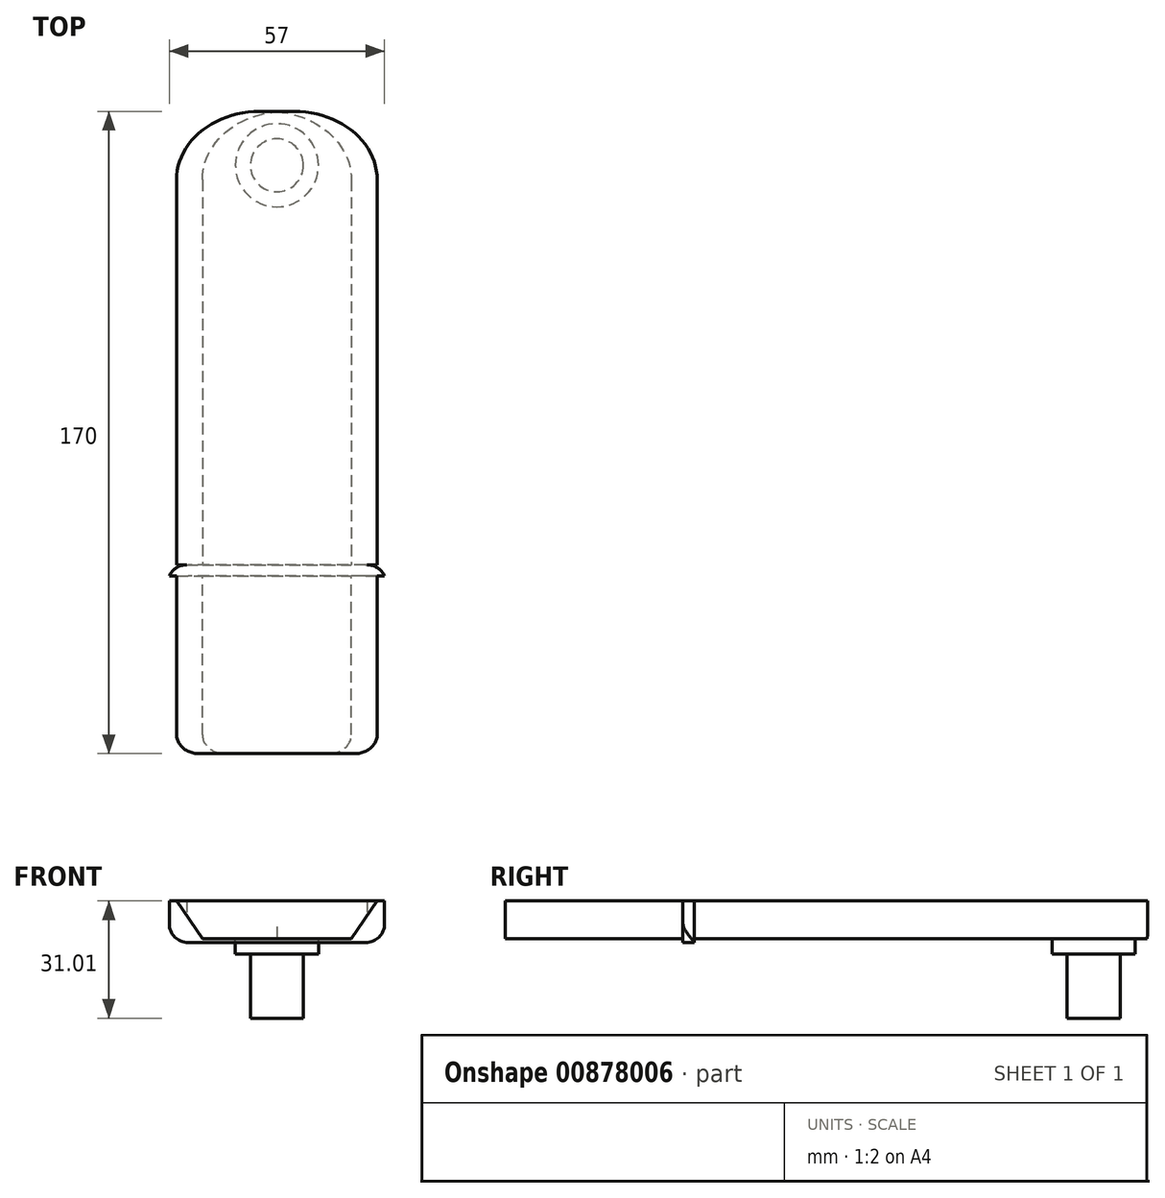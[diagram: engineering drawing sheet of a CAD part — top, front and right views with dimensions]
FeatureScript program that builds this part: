
annotation { "Feature Type Name" : "Feature", "Feature Type Description" : "" }
export const myFeature = defineFeature(function(context is Context, id is Id, definition is map)
    precondition{}
    {
        {
            var Q0;
            Q0=qCreatedBy(makeId("Front.planeOp"),FACE);
            var sketch = newSketch(context, id + "F0", { "sketchPlane" : qUnion([Q0])});
            skLineSegment(sketch, "E0.bottom", {"start": v(-20, -6.88) * mm, "end": v(20, -6.87) * mm});
            skLineSegment(sketch, "E1", {"start": v(27.5, 4.13) * mm, "end": v(20, -6.88) * mm});
            skLineSegment(sketch, "E2", {"start": v(-27.5, 4.12) * mm, "end": v(-20, -6.88) * mm});
            skLineSegment(sketch, "E3", {"start": v(-27.5, 4.12) * mm, "end": v(27.5, 4.13) * mm});
            skLineSegment(sketch, "E4.0", {"start": v(-27.5, 3.62) * mm, "end": v(27.5, 3.63) * mm});
            skLineSegment(sketch, "E5.0", {"start": v(-27.09, 4.4) * mm, "end": v(-19.59, -6.6) * mm});
            skLineSegment(sketch, "E6.0", {"start": v(-20, -6.38) * mm, "end": v(20, -6.37) * mm});
            skLineSegment(sketch, "E7.0", {"start": v(27.09, 4.4) * mm, "end": v(19.59, -6.6) * mm});
            skLineSegment(sketch, "E8.bottom", {"start": v(28.5, 3.63) * mm, "end": v(-28.5, 3.63) * mm});
            skLineSegment(sketch, "E8.top", {"start": v(28.5, -7.37) * mm, "end": v(-28.5, -7.38) * mm});
            skLineSegment(sketch, "E8.left", {"start": v(28.5, 3.63) * mm, "end": v(28.5, -7.37) * mm});
            skLineSegment(sketch, "E8.right", {"start": v(-28.5, 3.63) * mm, "end": v(-28.5, -7.38) * mm});
            skSolve(sketch);
        }
        {
            var Q0;
            {var subQ0=sQuery(id+"F0.wireOp",EDGE,"E5.0");var subQ1=sQuery(id+"F0.wireOp",EDGE,"E4.0");var subQ2=makeQuery(id+"F0.imprint","INTERSECT",VERTEX,{"derivedFrom":[subQ1,subQ0]});Q0=makeQuery(id+"F0.imprint","IMPRINT",FACE,{"disambiguationData":[TD([[makeQuery(id+"F0.imprint","IMPRINT",EDGE,{"disambiguationData":[TD([[subQ2,-1.0]])],"derivedFrom":subQ1}),-1.0]])]});}
            var Q1;
            {var subQ0=sQuery(id+"F0.wireOp",EDGE,"E6.0");var subQ1=sQuery(id+"F0.wireOp",EDGE,"E5.0");var subQ2=makeQuery(id+"F0.imprint","INTERSECT",VERTEX,{"derivedFrom":[subQ1,subQ0]});Q1=makeQuery(id+"F0.imprint","IMPRINT",FACE,{"disambiguationData":[TD([[makeQuery(id+"F0.imprint","IMPRINT",EDGE,{"disambiguationData":[TD([[subQ2,1.0]])],"derivedFrom":subQ1}),1.0]])]});}
            extrude(context, id + "F1", {"entities" : qUnion([Q0, Q1]), "depth" : 50 * mm, "offsetDistance" : 25 * mm});
        }
        {
            var Q0;
            {var subQ4=sQuery(id+"F0.wireOp",EDGE,"E0.bottom");Q0=makeQuery(id+"F0.imprint","IMPRINT",FACE,{"disambiguationData":[TD([[makeQuery(id+"F0.imprint","IMPRINT",EDGE,{"derivedFrom":subQ4}),-1.0]])]});}
            var Q1;
            {var subQ0=sQuery(id+"F0.wireOp",EDGE,"E6.0");var subQ1=sQuery(id+"F0.wireOp",EDGE,"E5.0");var subQ2=makeQuery(id+"F0.imprint","INTERSECT",VERTEX,{"derivedFrom":[subQ1,subQ0]});Q1=makeQuery(id+"F0.imprint","IMPRINT",FACE,{"disambiguationData":[TD([[makeQuery(id+"F0.imprint","IMPRINT",EDGE,{"disambiguationData":[TD([[subQ2,1.0]])],"derivedFrom":subQ1}),1.0]])]});}
            var Q2;
            {var subQ6=sQuery(id+"F0.wireOp",EDGE,"E0.bottom");Q2=makeQuery(id+"F0.imprint","IMPRINT",FACE,{"disambiguationData":[TD([[makeQuery(id+"F0.imprint","IMPRINT",EDGE,{"derivedFrom":subQ6}),1.0]])]});}
            extrude(context, id + "F2", {"entities" : qUnion([Q0, Q1, Q2]), "operationType" : NewBodyOperationType.ADD, "depth" : 3 * mm, "offsetDistance" : 25 * mm});
        }
        {
            var Q0;
            Q0=makeQuery(id+"F2.opExtrude","SWEPT_EDGE",EDGE,{"disambiguationData":[OSD([sQuery(id+"F0.wireOp",EDGE,"E8.top"),sQuery(id+"F0.wireOp",EDGE,"E8.left")])]});
            var Q1;
            Q1=makeQuery(id+"F2.opExtrude","SWEPT_EDGE",EDGE,{"disambiguationData":[OSD([sQuery(id+"F0.wireOp",EDGE,"E8.top"),sQuery(id+"F0.wireOp",EDGE,"E8.right")])]});
            var Q2;
            Q2=makeQuery(id+"F2.opExtrude","CAP_EDGE",EDGE,{"disambiguationData":[OSD([sQuery(id+"F0.wireOp",EDGE,"E8.left")])],"isStart":true});
            var Q3;
            Q3=makeQuery(id+"F2.opExtrude","CAP_EDGE",EDGE,{"disambiguationData":[OSD([sQuery(id+"F0.wireOp",EDGE,"E8.right")])],"isStart":true});
            fillet(context, id + "F3", {"entities" : qUnion([Q0, Q1, Q2, Q3]), "radius" : 5 * mm, "tangentPropagation" : true, "allowEdgeOverflow" : false});
        }
        {
            var Q0;
            {var subQ0=sQuery(id+"F0.wireOp",EDGE,"E6.0");var subQ1=sQuery(id+"F0.wireOp",EDGE,"E5.0");var subQ2=makeQuery(id+"F0.imprint","INTERSECT",VERTEX,{"derivedFrom":[subQ1,subQ0]});Q0=makeQuery(id+"F0.imprint","IMPRINT",FACE,{"disambiguationData":[TD([[makeQuery(id+"F0.imprint","IMPRINT",EDGE,{"disambiguationData":[TD([[subQ2,1.0]])],"derivedFrom":subQ1}),1.0]])]});}
            extrude(context, id + "F4", {"entities" : qUnion([Q0]), "operationType" : NewBodyOperationType.ADD, "oppositeDirection" : true, "depth" : 120 * mm, "offsetDistance" : 25 * mm});
        }
        {
            var Q0;
            Q0=makeQuery(id+"F4.opExtrude","CAP_EDGE",EDGE,{"disambiguationData":[OSD([sQuery(id+"F0.wireOp",EDGE,"E7.0")])],"isStart":false});
            var Q1;
            Q1=makeQuery(id+"F4.opExtrude","CAP_EDGE",EDGE,{"disambiguationData":[OSD([sQuery(id+"F0.wireOp",EDGE,"E5.0")])],"isStart":false});
            fillet(context, id + "F5", {"entities" : qUnion([Q0, Q1]), "radius" : 18.1 * mm, "tangentPropagation" : true, "allowEdgeOverflow" : false});
        }
        {
            var Q0;
            Q0=makeQuery(id+"F4.opExtrude","SWEPT_FACE",FACE,{"disambiguationData":[OSD([sQuery(id+"F0.wireOp",EDGE,"E6.0")])]});
            var sketch = newSketch(context, id + "F6", { "sketchPlane" : qUnion([Q0])});
            skCircle(sketch, "E9", {"center": v(0, -105.72) * mm, "radius": 11 * mm});
            skPoint(sketch, "E10", {"position": v(2.18, -83.79) * mm});
            skSolve(sketch);
        }
        {
            var Q0;
            Q0 = qSketchRegion(id + "F6", true);
            extrude(context, id + "F7", {"entities" : qUnion([Q0]), "operationType" : NewBodyOperationType.ADD, "depth" : 4 * mm, "offsetDistance" : 25 * mm});
        }
        {
            var Q0;
            Q0=makeQuery(id+"F7.opExtrude","CAP_FACE",FACE,{"disambiguationData":[OSD([sQuery(id+"F6.wireOp",EDGE,"E9")])],"isStart":false});
            var sketch = newSketch(context, id + "F8", { "sketchPlane" : qUnion([Q0])});
            skCircle(sketch, "E11", {"center": v(0, -105.72) * mm, "radius": 7 * mm});
            skSolve(sketch);
        }
        {
            var Q0;
            Q0=makeQuery(id+"F8.imprint","IMPRINT",FACE,{"disambiguationData":[TD([[makeQuery(id+"F8.imprint","IMPRINT",EDGE,{"derivedFrom":sQuery(id+"F8.wireOp",EDGE,"E11")}),1.0]])]});
            extrude(context, id + "F9", {"entities" : qUnion([Q0]), "operationType" : NewBodyOperationType.ADD, "depth" : 17 * mm, "offsetDistance" : 25 * mm});
        }
        {
            var Q0;
            Q0=makeQuery(id+"F1.opExtrude","CAP_EDGE",EDGE,{"disambiguationData":[OSD([sQuery(id+"F0.wireOp",EDGE,"E7.0")])],"isStart":false});
            var Q1;
            Q1=makeQuery(id+"F1.opExtrude","CAP_EDGE",EDGE,{"disambiguationData":[OSD([sQuery(id+"F0.wireOp",EDGE,"E5.0")])],"isStart":false});
            fillet(context, id + "F10", {"entities" : qUnion([Q0, Q1]), "radius" : 5 * mm, "tangentPropagation" : true, "allowEdgeOverflow" : false});
        }
    });
